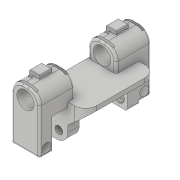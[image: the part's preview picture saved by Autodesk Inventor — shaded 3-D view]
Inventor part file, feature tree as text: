
AUTODESK INVENTOR PART (.ipt)
format: ipt  version: 2022 (Build 260153000, 153)  size: 884,224 bytes
history: native  units: in
note: dims shown in document units (in); Inventor stores cm internally (conversion verified against a paired STEP export)
features: projected_geometry x51, extrude x45, sketch x42, fillet x9, chamfer x2, pattern_linear x1, mirror x1
ambient origin geometry x8: Origin, YZ Plane, XZ Plane, XY Plane, X Axis, Y Axis, Z Axis, Center Point
bodies: Solid1 (feature_tree)
feature tree (151):
  extrude  "Extrusion1"  Depth=0.9843in
  extrude  "Extrusion2"  Depth=0.748in
  extrude  "Extrusion3"  Depth=0.4921in
  extrude  "Extrusion8"  Depth=0.2362in
  fillet  "Fillet1"  Radius=0.2362in
  fillet  "Fillet15"  Radius=1.006in
  extrude  "Extrusion50"  Depth=2.1654in
  extrude  "Extrusion52"  Depth=0.3937in TaperAngle=0.0deg
  extrude  "Extrusion53"  Depth=0.3937in
  fillet  "Fillet17"  Radius=1.2205in
  pattern_linear  "Rectangular Pattern2"  Spacing1=0.6299in  [1 undecoded]
  extrude  "Extrusion54"  Depth=0.6299in
  fillet  "Fillet18"  Radius=0.2697in
  mirror  "Mirror1"
  extrude  "Extrusion18"  Depth=0.0394in
  extrude  "Extrusion22"  Depth=0.0394in
  extrude  "Extrusion23"  Depth=0.3937in TaperAngle=0.0deg
  extrude  "Extrusion24"  Depth=0.0394in
  extrude  "Extrusion25"  Depth=0.0394in
  extrude  "Extrusion26"  Depth=0.0394in
  extrude  "Extrusion27"  Depth=0.3937in TaperAngle=0.0deg
  extrude  "Extrusion28"  Depth=0.0394in
  extrude  "Extrusion29"  Depth=0.0787in
  fillet  "Fillet3"  Radius=1.0in
  extrude  "Extrusion30"  Depth=0.0394in TaperAngle=0.0deg
  extrude  "Extrusion31"  Depth=0.0394in TaperAngle=0.0deg
  extrude  "Extrusion32"  Depth=0.6299in
  chamfer  "Chamfer1"  Angle=45.0deg  [1 undecoded]
  chamfer  "Chamfer2"  Distance=0.8661in
  extrude  "Extrusion33"  Depth=0.0787in TaperAngle=0.0deg
  extrude  "Extrusion34"  Depth=0.0394in
  extrude  "Extrusion35"  Depth=0.0394in
  extrude  "Extrusion36"  Depth=0.0394in
  extrude  "Extrusion37"  Depth=0.0394in TaperAngle=0.0deg
  extrude  "Extrusion38"  Depth=0.0394in
  extrude  "Extrusion39"  Depth=0.0394in TaperAngle=0.0deg
  extrude  "Extrusion41"  Depth=0.0394in
  extrude  "Extrusion42"  Depth=0.0394in
  extrude  "Extrusion43"  Depth=0.0394in TaperAngle=0.0deg
  extrude  "Extrusion44"  Depth=0.0394in
  extrude  "Extrusion45"  Depth=0.0394in
  extrude  "Extrusion46"  Depth=0.0394in TaperAngle=0.0deg
  extrude  "Extrusion47"  Depth=0.0394in TaperAngle=0.0deg
  extrude  "Extrusion48"  Depth=0.0394in TaperAngle=0.0deg
  extrude  "Extrusion49"  Depth=0.3937in
  fillet  "Fillet11"  Radius=0.3937in
  fillet  "Fillet13"  Radius=0.0787in
  fillet  "Fillet14"  Radius=0.0827in
  fillet  "Fillet16"  Radius=0.0827in
  extrude  "Extrusion51"  Depth=0.0394in
  extrude  "Extrusion55"  Depth=0.0394in
  extrude  "Extrusion56"  Depth=0.0394in
  extrude  "Extrusion57"  Depth=0.0394in
  extrude  "Extrusion58"  Depth=0.0394in TaperAngle=0.0deg
  extrude  "拉伸59"  Depth=0.0787in
  extrude  "拉伸60"  Depth=0.0787in
  extrude  "拉伸61"  TaperAngle=45.0deg  [1 undecoded]
  extrude  "拉伸62"  Depth=0.0787in
  sketch  "Sketch1"  dims[d0=0.9843in d1=0.0in d2=1.2205in]
  sketch  "Sketch3"  dims[d4=0.748in d5=0.0in d6=0.6063in]
  projected_geometry  "Projected Loop1"
  sketch  "Sketch4"  dims[d7=0.4331in d8=0.4921in]
  projected_geometry  "Projected Loop2"
  sketch  "Sketch5"  dims[d9=0.748in d10=0.0in d11=0.315in d15=0.2362in d19=1.006in]
  projected_geometry  "Projected Loop3"
  projected_geometry  "Projected Loop4"
  projected_geometry  "Projected Loop5"
  sketch  "Sketch16"  dims[d20=1.9488in d21=2.1654in]
  projected_geometry  "Projected Loop20"
  sketch  "Sketch20"  dims[d33=0.3937in d43=0.7874in d44=0.0in]
  projected_geometry  "Projected Loop25"
  projected_geometry  "Projected Loop26"
  sketch  "Sketch22"  dims[d109=0.3937in d110=0.7087in d112=1.2205in]
  sketch  "Sketch23"  dims[d113=1.0in d114=0.0in]
  projected_geometry  "Projected Loop27"
  projected_geometry  "Projected Loop28"
  projected_geometry  "Projected Loop29"
  projected_geometry  "Projected Loop30"
  sketch  "Sketch24"  dims[d130=0.0787in d131=0.0in]
  projected_geometry  "Projected Loop31"
  sketch  "Sketch25"  dims[d132=0.0787in d133=0.0in]
  projected_geometry  "Projected Loop32"
  sketch  "Sketch26"  dims[d134=0.0039in d135=0.0in]
  projected_geometry  "Projected Loop33"
  sketch  "Sketch27"  dims[d136=0.2879in d137=0.1181in d138=0.1181in d139=0.1181in d140=0.1181in d141=0.2879in d142=0.0591in d143=0.0591in d144=0.1181in d145=0.0394in d147=1.1329in]
  projected_geometry  "Projected Loop34"
  projected_geometry  "Projected Loop35"
  sketch  "Sketch28"  dims[d149=45.0deg]
  projected_geometry  "Projected Loop36"
  sketch  "Sketch29"  dims[d151=0.748in d152=0.0in]
  projected_geometry  "Projected Loop37"
  sketch  "Sketch30"  dims[d153=0.0039in d154=0.0in]
  projected_geometry  "Projected Loop38"
  sketch  "Sketch32"  dims[d155=0.1654in]
  projected_geometry  "Projected Loop40"
  sketch  "Sketch33"  dims[d156=0.1439in]
  projected_geometry  "Projected Loop41"
  sketch  "Sketch34"  dims[d157=0.5039in]
  projected_geometry  "Projected Loop42"
  projected_geometry  "Projected Loop43"
  projected_geometry  "Projected Loop44"
  sketch  "Sketch35"  dims[d158=0.1496in d159=0.0in]
  projected_geometry  "Projected Loop45"
  sketch  "Sketch36"  dims[d160=0.7077in]
  projected_geometry  "Projected Loop46"
  sketch  "Sketch38"  dims[d161=0.689in d162=0.0in]
  projected_geometry  "Projected Loop49"
  sketch  "Sketch41"  dims[d163=0.1654in]
  projected_geometry  "Projected Loop50"
  sketch  "Sketch43"  dims[d165=0.6289in]
  projected_geometry  "Projected Loop53"
  sketch  "Sketch44"  dims[d166=0.5039in]
  projected_geometry  "Projected Loop54"
  sketch  "Sketch45"  dims[d167=0.7795in d168=0.0in]
  projected_geometry  "Projected Loop55"
  sketch  "Sketch46"  dims[d169=0.125in]
  projected_geometry  "Projected Loop56"
  sketch  "Sketch47"  dims[d170=0.315in]
  projected_geometry  "Projected Loop57"
  projected_geometry  "Projected Loop58"
  projected_geometry  "Projected Loop59"
  projected_geometry  "Projected Loop60"
  projected_geometry  "Projected Loop61"
  sketch  "Sketch49"  dims[d171=0.0118in d172=0.0in]
  projected_geometry  "Projected Loop62"
  projected_geometry  "Projected Loop63"
  projected_geometry  "Projected Loop64"
  sketch  "Sketch50"  dims[d173=0.315in]
  projected_geometry  "Projected Loop65"
  projected_geometry  "Projected Loop66"
  projected_geometry  "Projected Loop67"
  sketch  "Sketch51"  dims[d174=0.0118in d175=0.0in]
  projected_geometry  "Projected Loop68"
  sketch  "Sketch52"  dims[d176=0.0118in d177=0.0in]
  projected_geometry  "Projected Loop73"
  sketch  "Sketch53"  dims[d178=0.2756in d179=0.1299in d180=45.0deg]
  projected_geometry  "Projected Loop74"
  sketch  "Sketch54"  dims[d181=0.1969in d182=0.2362in d183=45.0deg]
  projected_geometry  "Projected Loop75"
  sketch  "Sketch55"  dims[d184=0.0787in d185=0.0in]
  projected_geometry  "Projected Loop76"
  projected_geometry  "Projected Loop77"
  projected_geometry  "Projected Loop78"
  sketch  "Sketch56"  dims[d189=0.0394in]
  sketch  "Sketch57"  dims[d190=0.0394in]
  sketch  "Sketch58"  dims[d191=0.1575in]
  sketch  "Sketch59"  dims[d192=0.6299in d193=0.0in]
  sketch  "草图60"  dims[d196=0.3937in]
  sketch  "草图61"  dims[d197=0.3937in]
  sketch  "草图62"  dims[d198=1.685in]
  sketch  "草图63"  dims[d200=0.6299in d201=0.0in d202=0.6299in d203=0.6299in d204=0.2697in d205=0.315in d206=0.315in d207=0.3937in d208=0.0in d209=0.2697in d210=0.315in d211=0.315in d212=0.3937in d213=0.0in d214=0.0394in d215=0.0787in d217=1.0in d218=0.0in d219=0.4331in d220=0.0in d237=2.0in d238=0.0in d239=0.2879in d240=0.1181in d241=0.1181in d242=0.1181in d243=0.1181in d244=0.2879in d245=0.0591in d246=0.0591in d247=0.1181in d248=0.0394in d249=1.1329in d251=0.6299in d252=45.0deg d253=0.8661in d254=0.0in d255=0.0787in d256=0.0in d257=0.1654in d258=0.1439in d259=0.5039in d260=0.0394in d261=0.0in d262=0.7077in d263=0.8071in d264=0.0in d265=0.6289in d266=0.1654in d268=0.689in d269=0.0in d270=0.5039in d271=0.4646in d273=0.689in d274=0.0in d275=0.689in d276=0.0in d277=0.689in d278=0.0in d279=0.3937in d281=0.3937in d282=0.0787in d283=0.0827in d284=0.0827in d285=0.6378in d286=0.6378in d287=0.4764in d288=0.4764in d289=0.2402in d290=0.0in d291=0.0787in d292=0.0787in d293=45.0deg d294=0.0787in d295=0.2402in d296=0.0in d297=0.3543in d298=0.5512in d299=0.1575in d300=0.0394in d301=0.0in d302=0.0in d303=0.0472in d304=0.0335in d305=0.0661in d306=0.0394in d307=0.0394in d308=0.2441in d309=0.0in d310=0.0063in d311=2.7559in d313=0.0787in d314=0.2441in d315=0.0in d316=0.0197in d317=0.3791in d318=0.126in d319=0.0in d320=0.4244in d321=0.0362in d322=0.0in d323=0.3791in d324=0.126in d325=0.0in d326=0.424in d327=0.0362in d328=0.0in d329=2.3346in d330=0.0in d331=2.3346in d332=0.0in d334=135.0deg d335=0.5906in d336=0.0in d337=0.0394in d338=0.0in]
note: 3 required parameter values undecoded (feature->parameter linkage not recoverable at this tier; creation-order binding heuristic only, values carry confidence <= 0.55)
